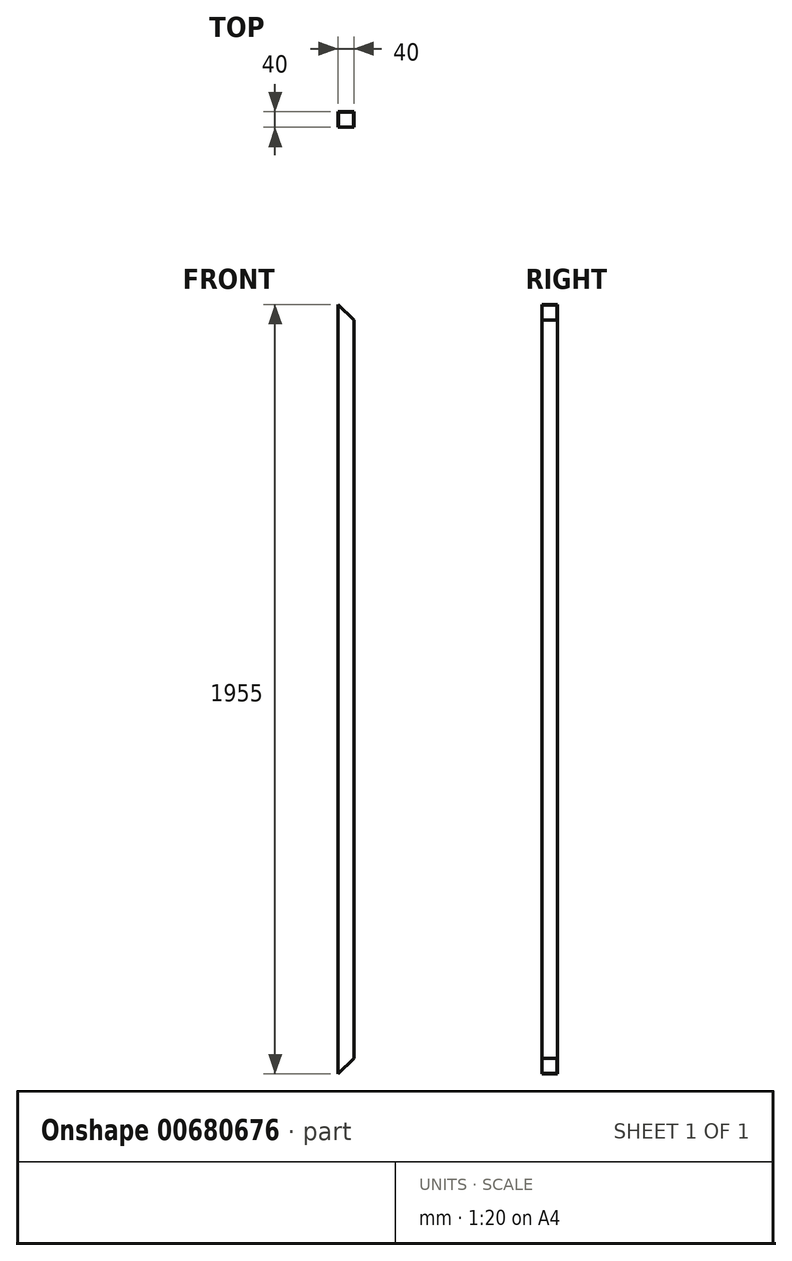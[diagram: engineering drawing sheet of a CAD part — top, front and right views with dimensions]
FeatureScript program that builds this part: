
annotation { "Feature Type Name" : "Feature", "Feature Type Description" : "" }
export const myFeature = defineFeature(function(context is Context, id is Id, definition is map)
    precondition{}
    {
        {
            var Q0;
            Q0=qCreatedBy(makeId("Top.planeOp"),FACE);
            var sketch = newSketch(context, id + "F0", { "sketchPlane" : qUnion([Q0])});
            skLineSegment(sketch, "E0.bottom", {"start": v(20, 20) * mm, "end": v(-20, 20) * mm});
            skLineSegment(sketch, "E0.top", {"start": v(20, -20) * mm, "end": v(-20, -20) * mm});
            skLineSegment(sketch, "E0.left", {"start": v(20, 20) * mm, "end": v(20, -20) * mm});
            skLineSegment(sketch, "E0.right", {"start": v(-20, 20) * mm, "end": v(-20, -20) * mm});
            skPoint(sketch, "E0.middle", {"position": v(0, 0) * mm});
            skLineSegment(sketch, "E1.bottom", {"start": v(19, 19) * mm, "end": v(-19, 19) * mm});
            skLineSegment(sketch, "E1.top", {"start": v(19, -19) * mm, "end": v(-19, -19) * mm});
            skLineSegment(sketch, "E1.left", {"start": v(19, 19) * mm, "end": v(19, -19) * mm});
            skLineSegment(sketch, "E1.right", {"start": v(-19, 19) * mm, "end": v(-19, -19) * mm});
            skSolve(sketch);
        }
        {
            var Q0;
            Q0=makeQuery(id+"F0.imprint","IMPRINT",FACE,{"disambiguationData":[TD([[makeQuery(id+"F0.imprint","IMPRINT",EDGE,{"derivedFrom":sQuery(id+"F0.wireOp",EDGE,"E0.bottom")}),1.0]])]});
            extrude(context, id + "F1", {"entities" : qUnion([Q0]), "endBound" : BoundingType.SYMMETRIC, "depth" : (2000 - 45) * mm, "offsetDistance" : 25 * mm});
        }
        {
            var Q0;
            Q0=makeQuery(id+"F1.opExtrude","SWEPT_FACE",FACE,{"disambiguationData":[OSD([sQuery(id+"F0.wireOp",EDGE,"E0.top")])]});
            var sketch = newSketch(context, id + "F2", { "sketchPlane" : qUnion([Q0])});
            skLineSegment(sketch, "E2", {"start": v(-20, 977.5) * mm, "end": v(20, 937.5) * mm});
            skLineSegment(sketch, "E3", {"start": v(-20, -977.5) * mm, "end": v(20, -937.5) * mm});
            skSolve(sketch);
        }
        {
            var Q0;
            {var subQ0=sQuery(id+"F2.wireOp",EDGE,"E3");Q0=makeQuery(id+"F2.imprint","IMPRINT",FACE,{"disambiguationData":[TD([[makeQuery(id+"F2.imprint","IMPRINT",EDGE,{"derivedFrom":subQ0}),-1.0]])]});}
            var Q1;
            {var subQ0=sQuery(id+"F2.wireOp",EDGE,"E2");Q1=makeQuery(id+"F2.imprint","IMPRINT",FACE,{"disambiguationData":[TD([[makeQuery(id+"F2.imprint","IMPRINT",EDGE,{"derivedFrom":subQ0}),1.0]])]});}
            extrude(context, id + "F3", {"entities" : qUnion([Q0, Q1]), "operationType" : NewBodyOperationType.REMOVE, "oppositeDirection" : true, "depth" : 100 * mm, "offsetDistance" : 25 * mm});
        }
    });
